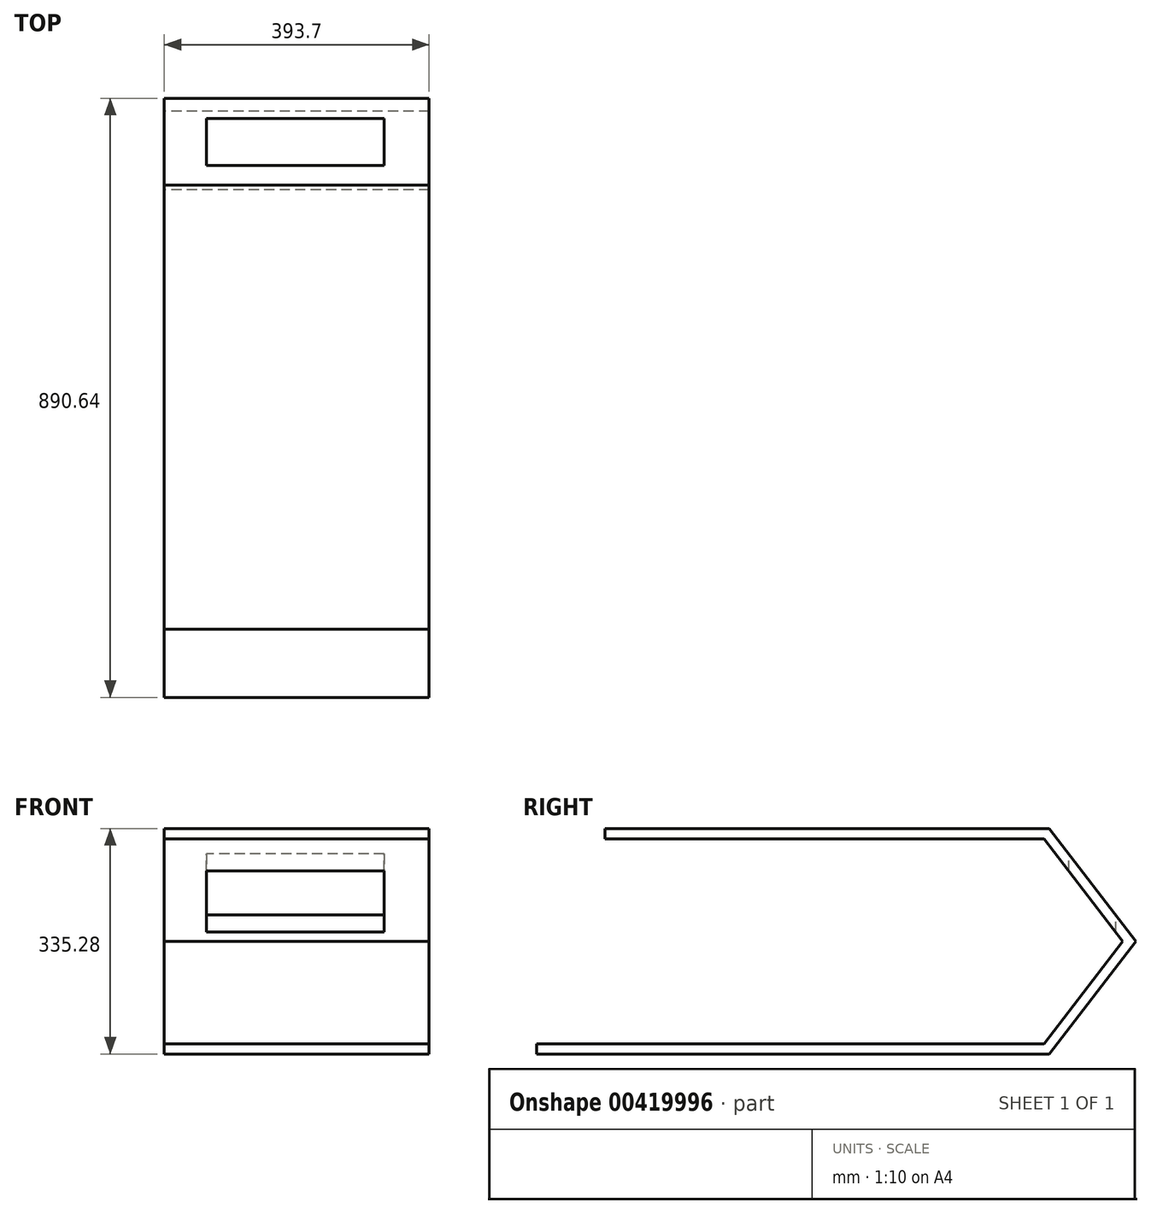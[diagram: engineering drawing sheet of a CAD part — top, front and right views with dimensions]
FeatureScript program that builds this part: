
annotation { "Feature Type Name" : "Feature", "Feature Type Description" : "" }
export const myFeature = defineFeature(function(context is Context, id is Id, definition is map)
    precondition{}
    {
        {
            var Q0;
            Q0=qCreatedBy(makeId("Right.planeOp"),FACE);
            var sketch = newSketch(context, id + "F0", { "sketchPlane" : qUnion([Q0])});
            skLineSegment(sketch, "E0", {"start": v(-538.89, 267.78) * mm, "end": v(-538.89, 252.54) * mm});
            skLineSegment(sketch, "E1", {"start": v(-538.89, 252.54) * mm, "end": v(114, 252.54) * mm});
            skLineSegment(sketch, "E2", {"start": v(114, 252.54) * mm, "end": v(230.94, 100.14) * mm});
            skLineSegment(sketch, "E3", {"start": v(230.94, 100.14) * mm, "end": v(114, -52.26) * mm});
            skLineSegment(sketch, "E4", {"start": v(114, -52.26) * mm, "end": v(-640.49, -52.26) * mm});
            skLineSegment(sketch, "E5", {"start": v(-640.49, -52.26) * mm, "end": v(-640.49, -67.5) * mm});
            skLineSegment(sketch, "E6", {"start": v(-640.49, -67.5) * mm, "end": v(121.51, -67.5) * mm});
            skLineSegment(sketch, "E7", {"start": v(121.51, -67.5) * mm, "end": v(250.15, 100.14) * mm});
            skLineSegment(sketch, "E8", {"start": v(250.15, 100.14) * mm, "end": v(121.51, 267.78) * mm});
            skLineSegment(sketch, "E9", {"start": v(121.51, 267.78) * mm, "end": v(-538.89, 267.78) * mm});
            skSolve(sketch);
        }
        {
            var Q0;
            Q0=makeQuery(id+"F0.imprint","IMPRINT",FACE,{"disambiguationData":[TD([[makeQuery(id+"F0.imprint","IMPRINT",EDGE,{"derivedFrom":sQuery(id+"F0.wireOp",EDGE,"E0")}),1.0]])]});
            extrude(context, id + "F1", {"entities" : qUnion([Q0]), "depth" : 393.7 * mm});
        }
        {
            var Q0;
            Q0=makeQuery(id+"F1.opExtrude","SWEPT_FACE",FACE,{"disambiguationData":[OSD([sQuery(id+"F0.wireOp",EDGE,"E9")])]});
            var sketch = newSketch(context, id + "F2", { "sketchPlane" : qUnion([Q0])});
            skLineSegment(sketch, "E10.bottom", {"start": v(62.59, 220.36) * mm, "end": v(326.8, 220.36) * mm});
            skLineSegment(sketch, "E10.top", {"start": v(62.59, 150.5) * mm, "end": v(326.8, 150.5) * mm});
            skLineSegment(sketch, "E10.left", {"start": v(62.59, 220.36) * mm, "end": v(62.59, 150.5) * mm});
            skLineSegment(sketch, "E10.right", {"start": v(326.8, 220.36) * mm, "end": v(326.8, 150.5) * mm});
            skSolve(sketch);
        }
        {
            var Q0;
            Q0=makeQuery(id+"F2.imprint","IMPRINT",FACE,{"disambiguationData":[TD([[makeQuery(id+"F2.imprint","IMPRINT",EDGE,{"derivedFrom":sQuery(id+"F2.wireOp",EDGE,"E10.bottom")}),-1.0]])]});
            extrude(context, id + "F3", {"entities" : qUnion([Q0]), "operationType" : NewBodyOperationType.REMOVE, "oppositeDirection" : true, "depth" : 154.94 * mm});
        }
    });
